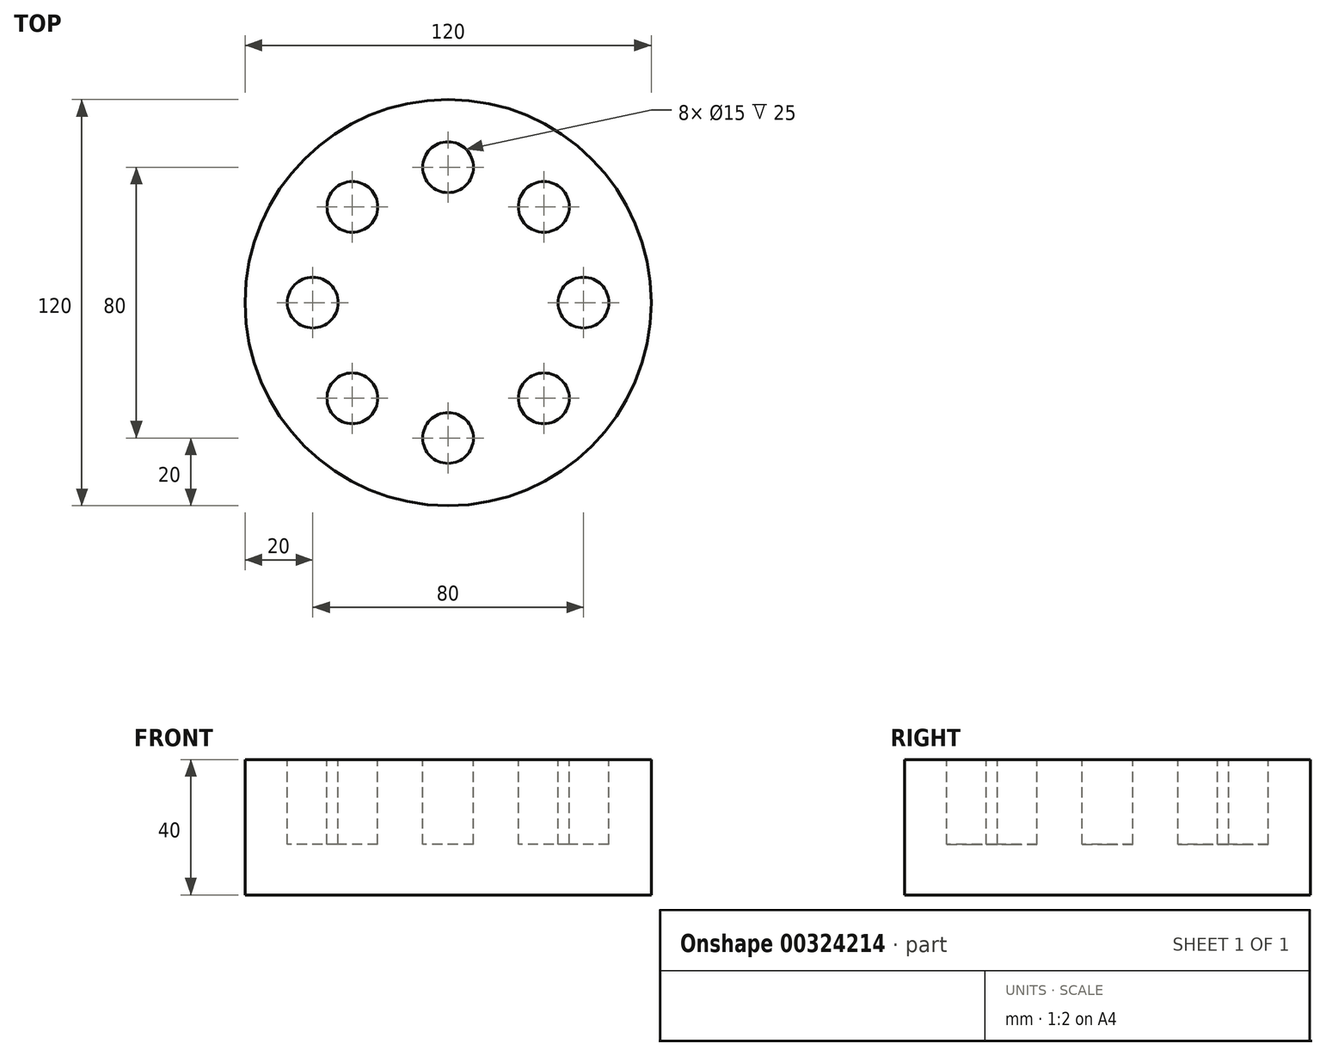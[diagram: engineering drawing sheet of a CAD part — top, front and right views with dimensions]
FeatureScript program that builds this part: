
annotation { "Feature Type Name" : "Feature", "Feature Type Description" : "" }
export const myFeature = defineFeature(function(context is Context, id is Id, definition is map)
    precondition{}
    {
        {
            var Q0;
            Q0=qCreatedBy(makeId("Top.planeOp"),FACE);
            var sketch = newSketch(context, id + "F0", { "sketchPlane" : qUnion([Q0])});
            skCircle(sketch, "E0", {"center": v(0, 0) * mm, "radius": 60 * mm});
            skSolve(sketch);
        }
        {
            var Q0;
            Q0=makeQuery(id+"F0.imprint","IMPRINT",FACE,{"disambiguationData":[TD([[makeQuery(id+"F0.imprint","IMPRINT",EDGE,{"derivedFrom":sQuery(id+"F0.wireOp",EDGE,"E0")}),1.0]])]});
            extrude(context, id + "F1", {"entities" : qUnion([Q0]), "depth" : 40 * mm});
        }
        {
            var Q0;
            Q0=makeQuery(id+"F1.opExtrude","CAP_FACE",FACE,{"disambiguationData":[OSD([sQuery(id+"F0.wireOp",EDGE,"E0")])],"isStart":false});
            var sketch = newSketch(context, id + "F2", { "sketchPlane" : qUnion([Q0])});
            skCircle(sketch, "E1", {"center": v(0, 40) * mm, "radius": 7.5 * mm});
            skCircle(sketch, "E2.1.0", {"center": v(-28.28, 28.28) * mm, "radius": 7.5 * mm});
            skCircle(sketch, "E2.2.0", {"center": v(-40, 0) * mm, "radius": 7.5 * mm});
            skCircle(sketch, "E2.3.0", {"center": v(-28.28, -28.28) * mm, "radius": 7.5 * mm});
            skCircle(sketch, "E2.4.0", {"center": v(0, -40) * mm, "radius": 7.5 * mm});
            skCircle(sketch, "E2.5.0", {"center": v(28.28, -28.28) * mm, "radius": 7.5 * mm});
            skCircle(sketch, "E2.6.0", {"center": v(40, 0) * mm, "radius": 7.5 * mm});
            skCircle(sketch, "E2.7.0", {"center": v(28.28, 28.28) * mm, "radius": 7.5 * mm});
            skPoint(sketch, "E2.center", {"position": v(0, 0) * mm});
            skSolve(sketch);
        }
        {
            var Q0;
            Q0=makeQuery(id+"F2.imprint","IMPRINT",FACE,{"disambiguationData":[TD([[makeQuery(id+"F2.imprint","IMPRINT",EDGE,{"derivedFrom":sQuery(id+"F2.wireOp",EDGE,"E2.1.0")}),1.0]])]});
            var Q1;
            Q1=makeQuery(id+"F2.imprint","IMPRINT",FACE,{"disambiguationData":[TD([[makeQuery(id+"F2.imprint","IMPRINT",EDGE,{"derivedFrom":sQuery(id+"F2.wireOp",EDGE,"E1")}),1.0]])]});
            var Q2;
            Q2=makeQuery(id+"F2.imprint","IMPRINT",FACE,{"disambiguationData":[TD([[makeQuery(id+"F2.imprint","IMPRINT",EDGE,{"derivedFrom":sQuery(id+"F2.wireOp",EDGE,"E2.7.0")}),1.0]])]});
            var Q3;
            Q3=makeQuery(id+"F2.imprint","IMPRINT",FACE,{"disambiguationData":[TD([[makeQuery(id+"F2.imprint","IMPRINT",EDGE,{"derivedFrom":sQuery(id+"F2.wireOp",EDGE,"E2.6.0")}),1.0]])]});
            var Q4;
            Q4=makeQuery(id+"F2.imprint","IMPRINT",FACE,{"disambiguationData":[TD([[makeQuery(id+"F2.imprint","IMPRINT",EDGE,{"derivedFrom":sQuery(id+"F2.wireOp",EDGE,"E2.5.0")}),1.0]])]});
            var Q5;
            Q5=makeQuery(id+"F2.imprint","IMPRINT",FACE,{"disambiguationData":[TD([[makeQuery(id+"F2.imprint","IMPRINT",EDGE,{"derivedFrom":sQuery(id+"F2.wireOp",EDGE,"E2.4.0")}),1.0]])]});
            var Q6;
            Q6=makeQuery(id+"F2.imprint","IMPRINT",FACE,{"disambiguationData":[TD([[makeQuery(id+"F2.imprint","IMPRINT",EDGE,{"derivedFrom":sQuery(id+"F2.wireOp",EDGE,"E2.3.0")}),1.0]])]});
            var Q7;
            Q7=makeQuery(id+"F2.imprint","IMPRINT",FACE,{"disambiguationData":[TD([[makeQuery(id+"F2.imprint","IMPRINT",EDGE,{"derivedFrom":sQuery(id+"F2.wireOp",EDGE,"E2.2.0")}),1.0]])]});
            extrude(context, id + "F3", {"entities" : qUnion([Q0, Q1, Q2, Q3, Q4, Q5, Q6, Q7]), "operationType" : NewBodyOperationType.REMOVE, "oppositeDirection" : true, "depth" : 25 * mm});
        }
    });
